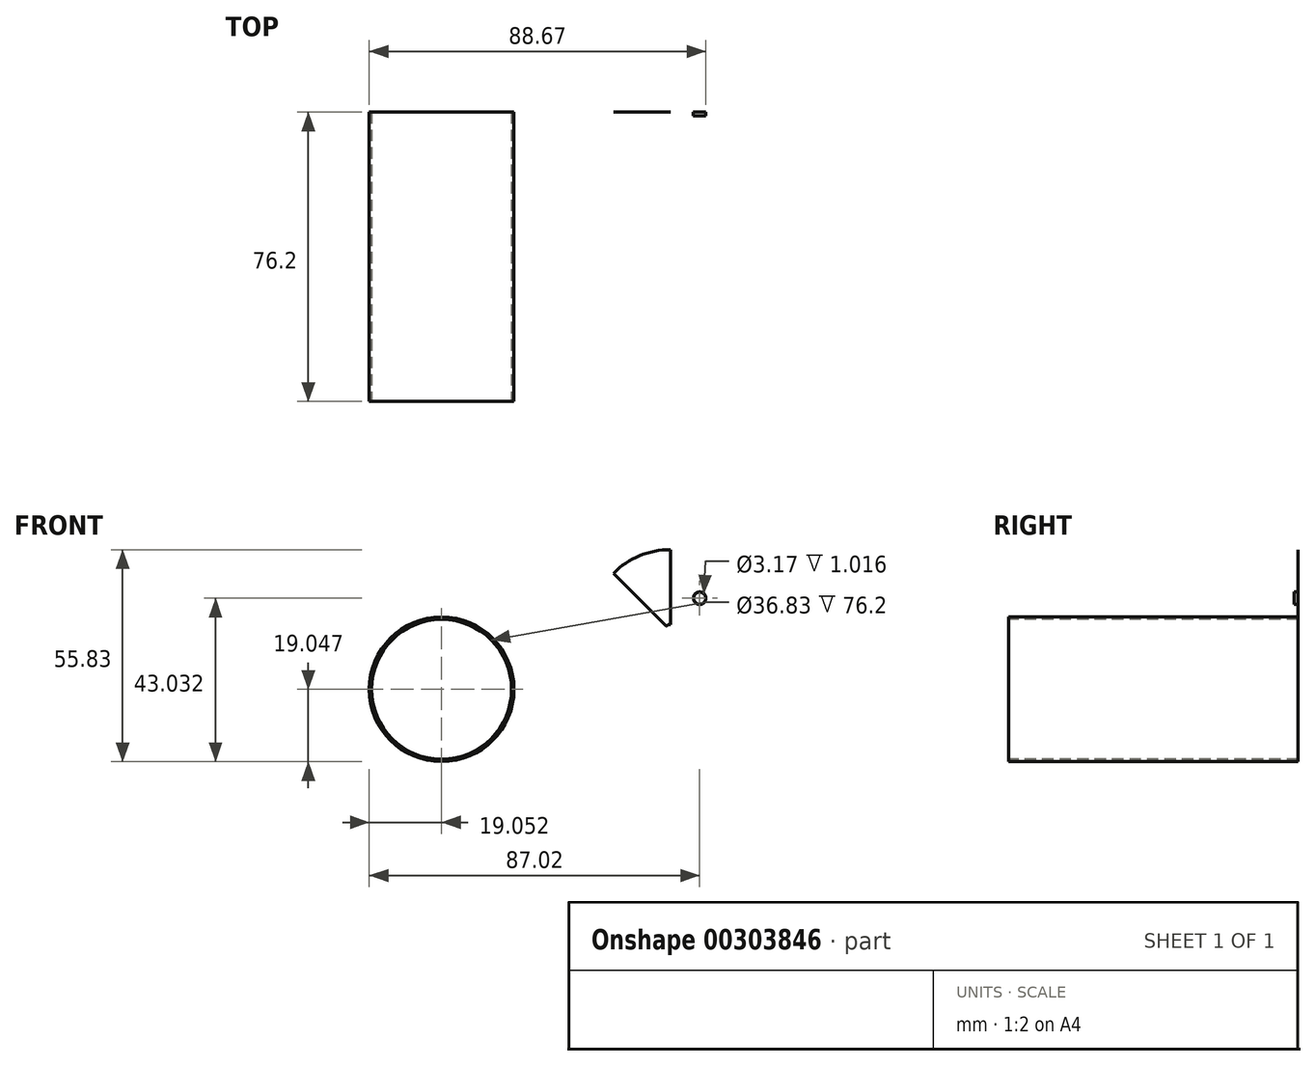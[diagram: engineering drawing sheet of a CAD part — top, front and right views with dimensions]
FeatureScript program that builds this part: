
annotation { "Feature Type Name" : "Feature", "Feature Type Description" : "" }
export const myFeature = defineFeature(function(context is Context, id is Id, definition is map)
    precondition{}
    {
        {
            var Q0;
            Q0=qCreatedBy(makeId("Front.planeOp"),FACE);
            var sketch = newSketch(context, id + "F0", { "sketchPlane" : qUnion([Q0])});
            skCircle(sketch, "E0", {"center": v(-13.16, 38.6) * mm, "radius": 19.05 * mm});
            skSolve(sketch);
        }
        {
            var Q0;
            Q0=makeQuery(id+"F0.imprint","IMPRINT",FACE,{"disambiguationData":[TD([[makeQuery(id+"F0.imprint","IMPRINT",EDGE,{"derivedFrom":sQuery(id+"F0.wireOp",EDGE,"E0")}),1.0]])]});
            extrude(context, id + "F1", {"entities" : qUnion([Q0]), "depth" : 76.2 * mm});
        }
        {
            var Q0;
            Q0=makeQuery(id+"F1.opExtrude","CAP_FACE",FACE,{"disambiguationData":[OSD([sQuery(id+"F0.wireOp",EDGE,"E0")])],"isStart":false});
            var sketch = newSketch(context, id + "F2", { "sketchPlane" : qUnion([Q0])});
            skLineSegment(sketch, "E1", {"start": v(-13.16, 38.6) * mm, "end": v(-1.86, 23.26) * mm});
            skSolve(sketch);
        }
        {
            var Q0;
            Q0=sQuery(id+"F2.wireOp",VERTEX,"E1.start");
            var Q1;
            Q1=makeQuery(id+"F1.opExtrude","SWEPT_BODY",BODY,{"disambiguationData":[OSD([sQuery(id+"F0.wireOp",EDGE,"E0")])]});
            hole(context, id + "F3", {"style" : HoleStyle.SIMPLE, "endStyle" : HoleEndStyle.BLIND, "holeDiameter" : 36.83 * mm, "holeDepth" : 76.2 * mm, "tappedDepth" : 12.7 * mm, "tapClearance" : 3, "locations" : qUnion([Q0]), "scope" : qUnion([Q1])});
        }
        {
            var Q0;
            Q0=qCreatedBy(makeId("Front.planeOp"),FACE);
            var sketch = newSketch(context, id + "F4", { "sketchPlane" : qUnion([Q0])});
            skArc(sketch, "E2", {"start": v(47.12, 75.38) * mm, "mid": v(38.98, 73.76) * mm, "end": v(32.08, 69.15) * mm});
            skLineSegment(sketch, "E3", {"start": v(47.12, 55.7) * mm, "end": v(47.12, 75.38) * mm});
            skArc(sketch, "E4", {"start": v(47.12, 55.7) * mm, "mid": v(46.52, 55.57) * mm, "end": v(46, 55.23) * mm});
            skLineSegment(sketch, "E5", {"start": v(46, 55.23) * mm, "end": v(32.08, 69.15) * mm});
            skSolve(sketch);
        }
        {
            var Q0;
            {var subQ1=sQuery(id+"F4.wireOp",EDGE,"yS0Cb7xk-fQjF-CrIj-hNPa-qPRxHhCkXTLj");var subQ3=sQuery(id+"F4.wireOp",EDGE,"E4");var subQ4=makeQuery(id+"F4.imprint","INTERSECT",VERTEX,{"derivedFrom":[subQ1,subQ3]});Q0=makeQuery(id+"F4.imprint","IMPRINT",FACE,{"disambiguationData":[TD([[makeQuery(id+"F4.imprint","IMPRINT",EDGE,{"disambiguationData":[TD([[subQ4,-1.0]])],"derivedFrom":subQ3}),1.0]])]});}
            var Q1;
            {var subQ1=sQuery(id+"F4.wireOp",EDGE,"yS0Cb7xk-fQjF-CrIj-hNPa-qPRxHhCkXTLj");var subQ3=sQuery(id+"F4.wireOp",EDGE,"E4");var subQ4=makeQuery(id+"F4.imprint","INTERSECT",VERTEX,{"derivedFrom":[subQ1,subQ3]});Q1=makeQuery(id+"F4.imprint","IMPRINT",FACE,{"disambiguationData":[TD([[makeQuery(id+"F4.imprint","IMPRINT",EDGE,{"disambiguationData":[TD([[subQ4,1.0]])],"derivedFrom":subQ3}),1.0]])]});}
            var Q2;
            {var subQ1=sQuery(id+"F4.wireOp",EDGE,"3oqZYfFd-3qWy-S12E-wYIz-GAf0wvdWtH6O");var subQ3=sQuery(id+"F4.wireOp",EDGE,"E4");var subQ4=makeQuery(id+"F4.imprint","INTERSECT",VERTEX,{"derivedFrom":[subQ1,subQ3]});Q2=makeQuery(id+"F4.imprint","IMPRINT",FACE,{"disambiguationData":[TD([[makeQuery(id+"F4.imprint","IMPRINT",EDGE,{"disambiguationData":[TD([[subQ4,-1.0]])],"derivedFrom":subQ3}),1.0]])]});}
            var Q3;
            {var subQ1=sQuery(id+"F4.wireOp",EDGE,"3oqZYfFd-3qWy-S12E-wYIz-GAf0wvdWtH6O");var subQ3=sQuery(id+"F4.wireOp",EDGE,"E4");var subQ4=makeQuery(id+"F4.imprint","INTERSECT",VERTEX,{"derivedFrom":[subQ1,subQ3]});Q3=makeQuery(id+"F4.imprint","IMPRINT",FACE,{"disambiguationData":[TD([[makeQuery(id+"F4.imprint","IMPRINT",EDGE,{"disambiguationData":[TD([[subQ4,1.0]])],"derivedFrom":subQ3}),1.0]])]});}
            var Q4;
            {var subQ1=sQuery(id+"F4.wireOp",EDGE,"illEdQMH-lDyQ-5zje-xBsS-e35VKA1LjoyA");var subQ3=sQuery(id+"F4.wireOp",EDGE,"E4");var subQ4=makeQuery(id+"F4.imprint","INTERSECT",VERTEX,{"derivedFrom":[subQ1,subQ3]});Q4=makeQuery(id+"F4.imprint","IMPRINT",FACE,{"disambiguationData":[TD([[makeQuery(id+"F4.imprint","IMPRINT",EDGE,{"disambiguationData":[TD([[subQ4,-1.0]])],"derivedFrom":subQ3}),1.0]])]});}
            var Q5;
            {var subQ1=sQuery(id+"F4.wireOp",EDGE,"illEdQMH-lDyQ-5zje-xBsS-e35VKA1LjoyA");var subQ3=sQuery(id+"F4.wireOp",EDGE,"E4");var subQ4=makeQuery(id+"F4.imprint","INTERSECT",VERTEX,{"derivedFrom":[subQ1,subQ3]});Q5=makeQuery(id+"F4.imprint","IMPRINT",FACE,{"disambiguationData":[TD([[makeQuery(id+"F4.imprint","IMPRINT",EDGE,{"disambiguationData":[TD([[subQ4,1.0]])],"derivedFrom":subQ3}),1.0]])]});}
            var Q6;
            {var subQ1=sQuery(id+"F4.wireOp",EDGE,"E3");var subQ3=sQuery(id+"F4.wireOp",EDGE,"E4");var subQ4=makeQuery(id+"F4.imprint","INTERSECT",VERTEX,{"derivedFrom":[subQ1,subQ3]});Q6=makeQuery(id+"F4.imprint","IMPRINT",FACE,{"disambiguationData":[TD([[makeQuery(id+"F4.imprint","IMPRINT",EDGE,{"disambiguationData":[TD([[subQ4,-1.0]])],"derivedFrom":subQ3}),1.0]])]});}
            var Q7;
            {var subQ1=sQuery(id+"F4.wireOp",EDGE,"E3");var subQ3=sQuery(id+"F4.wireOp",EDGE,"E4");var subQ4=makeQuery(id+"F4.imprint","INTERSECT",VERTEX,{"derivedFrom":[subQ1,subQ3]});Q7=makeQuery(id+"F4.imprint","IMPRINT",FACE,{"disambiguationData":[TD([[makeQuery(id+"F4.imprint","IMPRINT",EDGE,{"disambiguationData":[TD([[subQ4,1.0]])],"derivedFrom":subQ3}),1.0]])]});}
            var Q8;
            {var subQ0=sQuery(id+"F4.wireOp",EDGE,"yS0Cb7xk-fQjF-CrIj-hNPa-qPRxHhCkXTLj");var subQ1=sQuery(id+"F4.wireOp",EDGE,"E2");var subQ2=makeQuery(id+"F4.imprint","INTERSECT",VERTEX,{"derivedFrom":[subQ1,subQ0]});Q8=makeQuery(id+"F4.imprint","IMPRINT",FACE,{"disambiguationData":[TD([[makeQuery(id+"F4.imprint","IMPRINT",EDGE,{"disambiguationData":[TD([[subQ2,1.0]])],"derivedFrom":subQ1}),1.0]])]});}
            var Q9;
            {var subQ0=sQuery(id+"F4.wireOp",EDGE,"illEdQMH-lDyQ-5zje-xBsS-e35VKA1LjoyA");var subQ1=sQuery(id+"F4.wireOp",EDGE,"E2");var subQ2=makeQuery(id+"F4.imprint","INTERSECT",VERTEX,{"derivedFrom":[subQ1,subQ0]});Q9=makeQuery(id+"F4.imprint","IMPRINT",FACE,{"disambiguationData":[TD([[makeQuery(id+"F4.imprint","IMPRINT",EDGE,{"disambiguationData":[TD([[subQ2,1.0]])],"derivedFrom":subQ1}),1.0]])]});}
            var Q10;
            {var subQ0=sQuery(id+"F4.wireOp",EDGE,"E3");var subQ1=sQuery(id+"F4.wireOp",EDGE,"E2");var subQ2=makeQuery(id+"F4.imprint","INTERSECT",VERTEX,{"derivedFrom":[subQ1,subQ0]});Q10=makeQuery(id+"F4.imprint","IMPRINT",FACE,{"disambiguationData":[TD([[makeQuery(id+"F4.imprint","IMPRINT",EDGE,{"disambiguationData":[TD([[subQ2,1.0]])],"derivedFrom":subQ1}),1.0]])]});}
            var Q11;
            {var subQ0=sQuery(id+"F4.wireOp",EDGE,"3oqZYfFd-3qWy-S12E-wYIz-GAf0wvdWtH6O");var subQ1=sQuery(id+"F4.wireOp",EDGE,"E2");var subQ2=makeQuery(id+"F4.imprint","INTERSECT",VERTEX,{"derivedFrom":[subQ1,subQ0]});Q11=makeQuery(id+"F4.imprint","IMPRINT",FACE,{"disambiguationData":[TD([[makeQuery(id+"F4.imprint","IMPRINT",EDGE,{"disambiguationData":[TD([[subQ2,1.0]])],"derivedFrom":subQ1}),1.0]])]});}
            extrude(context, id + "F5", {"entities" : qUnion([Q0, Q1, Q2, Q3, Q4, Q5, Q6, Q7, Q8, Q9, Q10, Q11]), "depth" : 1 / 635 * mm});
        }
        {
            var Q0;
            Q0=makeQuery(id+"F5.opExtrude","CAP_FACE",FACE,{"disambiguationData":[OSD([sQuery(id+"F4.wireOp",EDGE,"E2"),sQuery(id+"F4.wireOp",EDGE,"yS0Cb7xk-fQjF-CrIj-hNPa-qPRxHhCkXTLj"),sQuery(id+"F4.wireOp",EDGE,"illEdQMH-lDyQ-5zje-xBsS-e35VKA1LjoyA"),sQuery(id+"F4.wireOp",EDGE,"E3"),sQuery(id+"F4.wireOp",EDGE,"3oqZYfFd-3qWy-S12E-wYIz-GAf0wvdWtH6O"),sQuery(id+"F4.wireOp",EDGE,"5zL6kDxW-ANPq-b6Vc-SWtz-imJhYLbccoKP"),sQuery(id+"F4.wireOp",EDGE,"tvCEqK39-1tjH-hwsp-FgsH-YLytVIuczk3a"),sQuery(id+"F4.wireOp",EDGE,"odgECVXb-nkm2-FkWc-HAce-WO67wnUcT8Ff"),sQuery(id+"F4.wireOp",EDGE,"bIsIDpOx-t1mZ-XgWb-WyQ0-zN9s9INGNsij"),sQuery(id+"F4.wireOp",EDGE,"E4")])],"isStart":false});
            var sketch = newSketch(context, id + "F6", { "sketchPlane" : qUnion([Q0])});
            skCircle(sketch, "E6", {"center": v(47.12, 54.1) * mm, "radius": 1.02 * mm});
            skSolve(sketch);
        }
        {
            var Q0;
            Q0=sQuery(id+"F6.wireOp",VERTEX,"E6.center");
            var Q1;
            Q1=makeQuery(id+"F5.opExtrude","SWEPT_BODY",BODY,{"disambiguationData":[OSD([sQuery(id+"F4.wireOp",EDGE,"E2"),sQuery(id+"F4.wireOp",EDGE,"yS0Cb7xk-fQjF-CrIj-hNPa-qPRxHhCkXTLj"),sQuery(id+"F4.wireOp",EDGE,"illEdQMH-lDyQ-5zje-xBsS-e35VKA1LjoyA"),sQuery(id+"F4.wireOp",EDGE,"E3"),sQuery(id+"F4.wireOp",EDGE,"3oqZYfFd-3qWy-S12E-wYIz-GAf0wvdWtH6O"),sQuery(id+"F4.wireOp",EDGE,"5zL6kDxW-ANPq-b6Vc-SWtz-imJhYLbccoKP"),sQuery(id+"F4.wireOp",EDGE,"tvCEqK39-1tjH-hwsp-FgsH-YLytVIuczk3a"),sQuery(id+"F4.wireOp",EDGE,"odgECVXb-nkm2-FkWc-HAce-WO67wnUcT8Ff"),sQuery(id+"F4.wireOp",EDGE,"bIsIDpOx-t1mZ-XgWb-WyQ0-zN9s9INGNsij"),sQuery(id+"F4.wireOp",EDGE,"E4")])]});
            hole(context, id + "F7", {"style" : HoleStyle.SIMPLE, "endStyle" : HoleEndStyle.BLIND, "holeDiameter" : 3.05 * mm, "holeDepth" : 76.2 * mm, "tappedDepth" : 12.7 * mm, "tapClearance" : 3, "locations" : qUnion([Q0]), "scope" : qUnion([Q1])});
        }
        {
            var Q0;
            Q0=qCreatedBy(makeId("Front.planeOp"),FACE);
            var sketch = newSketch(context, id + "F8", { "sketchPlane" : qUnion([Q0])});
            skCircle(sketch, "E7", {"center": v(54.81, 62.58) * mm, "radius": 1.65 * mm});
            skCircle(sketch, "E8", {"center": v(54.81, 62.58) * mm, "radius": 1.59 * mm});
            skSolve(sketch);
        }
        {
            var Q0;
            Q0=makeQuery(id+"F8.imprint","IMPRINT",FACE,{"disambiguationData":[TD([[makeQuery(id+"F8.imprint","IMPRINT",EDGE,{"derivedFrom":sQuery(id+"F8.wireOp",EDGE,"E7")}),1.0]])]});
            extrude(context, id + "F9", {"entities" : qUnion([Q0]), "depth" : 1.02 * mm});
        }
    });
